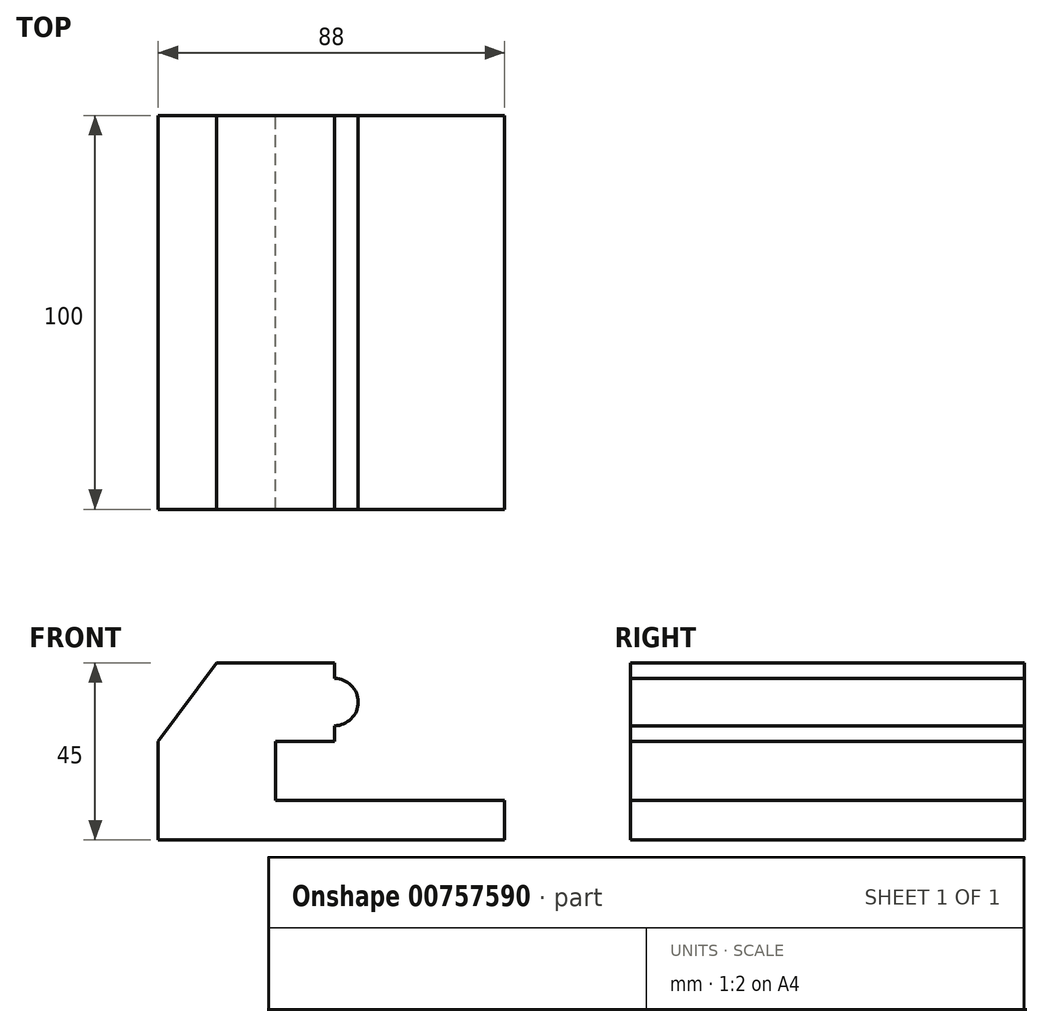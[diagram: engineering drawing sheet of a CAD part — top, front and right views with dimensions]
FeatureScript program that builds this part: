
annotation { "Feature Type Name" : "Feature", "Feature Type Description" : "" }
export const myFeature = defineFeature(function(context is Context, id is Id, definition is map)
    precondition{}
    {
        {
            var Q0;
            Q0=qCreatedBy(makeId("Front.planeOp"),FACE);
            var sketch = newSketch(context, id + "F0", { "sketchPlane" : qUnion([Q0])});
            skLineSegment(sketch, "E0", {"start": v(0, 0) * mm, "end": v(0, 25) * mm});
            skLineSegment(sketch, "E1", {"start": v(0, 25) * mm, "end": v(14.8, 45) * mm});
            skLineSegment(sketch, "E2", {"start": v(14.8, 45) * mm, "end": v(44.8, 45) * mm});
            skLineSegment(sketch, "E3", {"start": v(0, 0) * mm, "end": v(88, 0) * mm});
            skLineSegment(sketch, "E4", {"start": v(88, 0) * mm, "end": v(88, 10) * mm});
            skLineSegment(sketch, "E5", {"start": v(88, 10) * mm, "end": v(29.8, 10) * mm});
            skLineSegment(sketch, "E6", {"start": v(29.8, 10) * mm, "end": v(29.8, 25) * mm});
            skLineSegment(sketch, "E7", {"start": v(29.8, 25) * mm, "end": v(44.8, 25) * mm});
            skCircle(sketch, "E8", {"center": v(44.8, 35) * mm, "radius": 6 * mm});
            skLineSegment(sketch, "E9", {"start": v(44.8, 45) * mm, "end": v(44.8, 41) * mm});
            skLineSegment(sketch, "E10", {"start": v(44.8, 25) * mm, "end": v(44.8, 29) * mm});
            skSolve(sketch);
        }
        {
            var Q0;
            Q0 = qSketchRegion(id + "F0", true);
            extrude(context, id + "F1", {"entities" : qUnion([Q0]), "depth" : 100 * mm, "offsetDistance" : 25 * mm});
        }
    });
